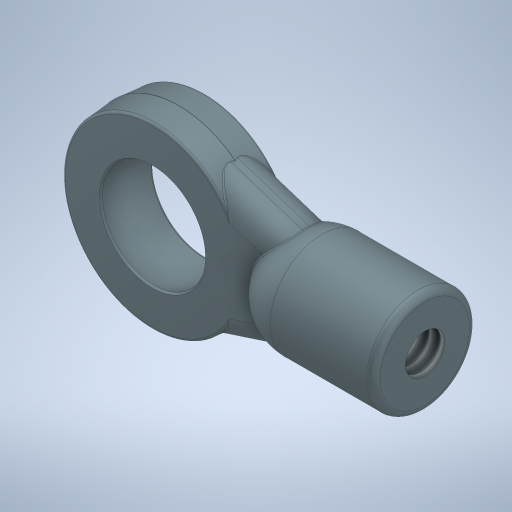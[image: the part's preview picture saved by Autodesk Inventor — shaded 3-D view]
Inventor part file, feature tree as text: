
AUTODESK INVENTOR PART (.ipt)
format: ipt  version: 2024 (Build 280153000, 153)  size: 494,080 bytes
history: native  units: in
note: dims shown in document units (in); Inventor stores cm internally (conversion verified against a paired STEP export)
features: sketch x5, fillet x3, projected_geometry x3, extrude x2, revolve x2, draft x2, split x1, hole x1, plane x1, chamfer x1, direct_edit x1, other x1
ambient origin geometry x8: Origin, YZ Plane, XZ Plane, XY Plane, X Axis, Y Axis, Z Axis, Center Point
bodies: Solid1 (feature_tree)
feature tree (23):
  extrude  "Extrusion1"  Depth=0.115in TaperAngle=0.0deg
  revolve  "Revolution1"  [1 undecoded]
  extrude  "Extrusion2"  Depth=0.1375in
  fillet  "Fillet1"  Radius=0.3961in
  split  "Split1"
  draft  "FaceDraft1"
  draft  "FaceDraft2"
  hole  "Hole1"  [1 undecoded]
  fillet  "Fillet2"  Radius=0.05in
  fillet  "Fillet3"  Radius=0.0344in
  plane  "Work Plane1"
  revolve  "Revolution2"  [1 undecoded]
  chamfer  "Chamfer1"  Distance=0.005in
  direct_edit  "Direct Edit1"
  sketch  "Sketch1"  dims[d0=0.4in d1=0.115in d2=0.0in]
  sketch  "Sketch2"  dims[d3=0.1125in d4=0.225in]
  sketch  "Sketch3"  dims[d5=90.0deg d6=0.1375in d7=0.3961in]
  sketch  "Sketch4"  dims[d8=0.3154in d9=0.115in d10=0.0in d11=0.05in d12=0.0344in]
  sketch  "Sketch5"  dims[d13=0.0344in d14=0.0849in d15=0.224in d16=0.375in d17=0.25in d18=0.5635in d19=0.225in d20=0.8108in d21=0.015in d22=0.005in d23=0.25in d24=90.0deg d25=0.005in d26=0.125in d27=45.0deg d28=3.937in d29=0.3937in d30=0.3937in]
  projected_geometry  "Project Cut Edges1"
  projected_geometry  "Project Cut Edges2"
  projected_geometry  "Project Cut Edges3"
  other  "Scale1"
note: 3 required parameter values undecoded (feature->parameter linkage not recoverable at this tier; creation-order binding heuristic only, values carry confidence <= 0.55)